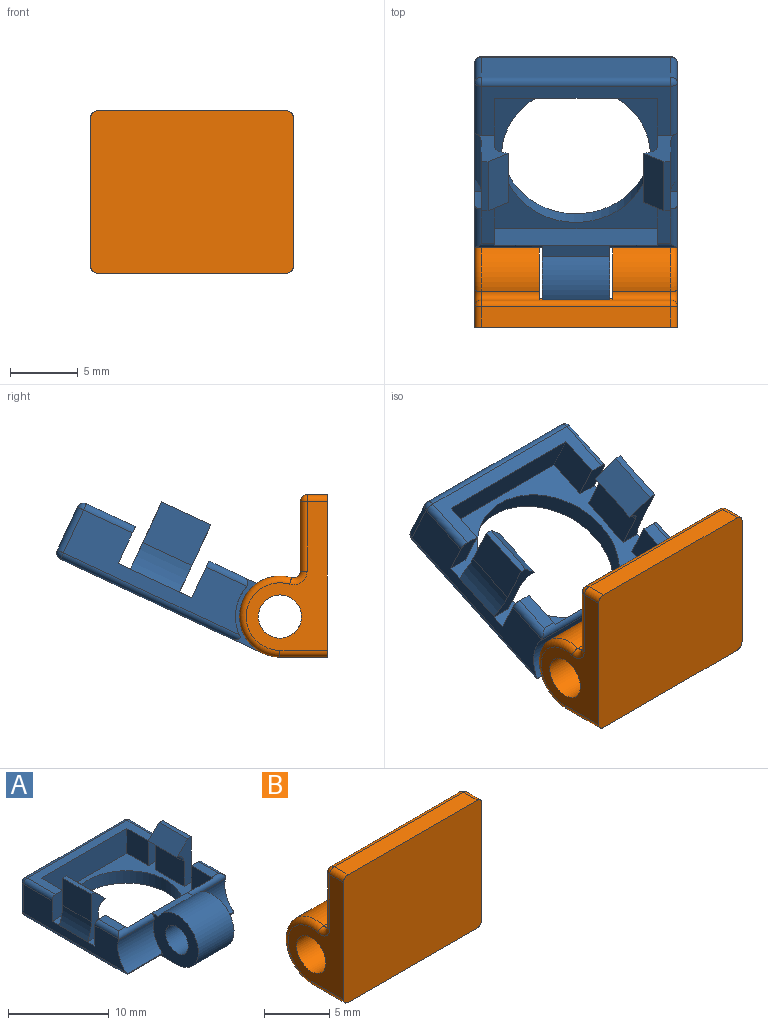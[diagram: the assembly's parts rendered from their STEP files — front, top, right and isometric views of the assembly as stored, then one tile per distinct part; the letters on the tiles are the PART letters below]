
ASSEMBLY  parts=2 mates=1
PART A: 60 faces, bbox 15x20x7 mm
  f0: plane 5x0.9mm, normal (0,0,1), area 4.5mm2, adj f2,f3,f15,f40
  f1: plane 2.83x1mm, normal (0,0,1), area 2.8mm2, adj f16,f27,f44,f45
  f2: plane 6.5x6mm, normal (-1,0,0), area 22.2mm2, adj f0,f15,f17,f38,f40,f41,f45,f59
  f3: plane 6.5x6mm, normal (1,0,0), area 22.2mm2, adj f0,f15,f17,f39,f40,f41,f43,f47
  f4: plane 2.83x1mm, normal (0,0,1), area 2.8mm2, adj f14,f23,f42,f43
  f5: plane 4x3mm, normal (1,0,0), area 12mm2, adj f19,f25,f28,f34
  f6: plane 4x3mm, normal (-1,0,0), area 12mm2, adj f19,f20,f22,f35
  f7: plane 14.35x3.5mm, normal (-1,0,0), area 32.1mm2, adj f19,f26,f27,f37,f38,f44,f45,f52
  f8: plane 3x3mm, normal (-1,0,0), area 9mm2, adj f10,f13,f19,f24
  f9: plane 3x3mm, normal (1,0,0), area 9mm2, adj f10,f13,f19,f26
  f10: plane 14x4mm, normal (0,0,1), area 20mm2, adj f8,f9,f13,f24,f26,f46,f51,f52
  f11: plane 14.35x3.5mm, normal (1,0,0), area 32.1mm2, adj f19,f23,f24,f36,f39,f42,f43,f46
  f12: plane 14x3.5mm, normal (0,1,0), area 49mm2, adj f50,f51,f55,f56
  f13: plane 12x3mm, normal (0,-1,0), area 36mm2, adj f8,f9,f10,f19
  f14: plane 3x3mm, normal (-1,0,0), area 9mm2, adj f4,f15,f19,f23,f43
  f15: plane 12x3mm, normal (0,1,0), area 35.8mm2, adj f0,f2,f3,f14,f16,f19,f43,f45
  f16: plane 3x3mm, normal (1,0,0), area 9mm2, adj f1,f15,f19,f27,f45
  f17: plane 16.5x14mm, normal (0,0,-1), area 113.6mm2, adj f2,f3,f18,f40,f47,f49,f55,f58
  f18: cylinder r=5.5mm len=11mm, axis (0,0,-1), area 51.8mm2, adj f17,f19
  f19: plane 15x12mm, normal (0,0,1), area 55mm2, adj f5,f6,f7,f8,f9,f11,f13,f14
  f20: plane 5.5x2.5mm, normal (0,1,0), area 6.4mm2, adj f6,f19,f21,f30,f32,f35,f36
  f21: plane 4x3.32mm, normal (1,0,0), area 13.3mm2, adj f20,f22,f30,f36
  f22: plane 5.5x2.5mm, normal (0,-1,0), area 6.4mm2, adj f6,f19,f21,f30,f32,f35,f36
  f23: plane 3x1.5mm, normal (0,1,0), area 4.4mm2, adj f4,f11,f14,f19,f42
  f24: plane 3x1.5mm, normal (0,-1,0), area 4.4mm2, adj f8,f10,f11,f19,f46
  f25: plane 5.5x2.5mm, normal (0,1,0), area 6.4mm2, adj f5,f19,f29,f31,f33,f34,f37
  f26: plane 3x1.5mm, normal (0,-1,0), area 4.4mm2, adj f7,f9,f10,f19,f52
  f27: plane 3x1.5mm, normal (0,1,0), area 4.4mm2, adj f1,f7,f16,f19,f44
  f28: plane 5.5x2.5mm, normal (0,-1,0), area 6.4mm2, adj f5,f19,f29,f31,f33,f34,f37
  f29: plane 4x3.32mm, normal (-1,0,0), area 13.3mm2, adj f25,f28,f31,f37
  f30: plane 4x0.5mm, normal (0,0,1), area 2mm2, adj f20,f21,f22,f32
  f31: plane 4x0.5mm, normal (0,0,1), area 2mm2, adj f25,f28,f29,f33
  f32: plane 4x1.5mm, normal (-0.71,0,0.71), area 8.5mm2, adj f20,f22,f30,f35
  f33: plane 4x1.5mm, normal (0.71,0,0.71), area 8.5mm2, adj f25,f28,f31,f34
  f34: cylinder r=1mm len=4mm, axis (0,-1,0), area 6.3mm2, adj f5,f25,f28,f33
  f35: cylinder r=1mm len=4mm, axis (0,-1,0), area 6.3mm2, adj f6,f20,f22,f32
  f36: cylinder r=5mm len=4mm, axis (0,-1,0), area 9mm2, adj f11,f20,f21,f22
  f37: cylinder r=5mm len=4mm, axis (0,-1,0), area 9mm2, adj f7,f25,f28,f29
  f38: cylinder r=3.3mm len=5mm, axis (1,0,0), area 19.6mm2, adj f2,f7,f45,f58,f59
  f39: cylinder r=3.3mm len=5mm, axis (-1,0,0), area 19.6mm2, adj f3,f11,f43,f47,f49
  f40: cylinder r=3mm len=6mm, axis (-1,0,0), area 62.8mm2, adj f0,f2,f3,f17
  f41: cylinder r=1.6mm len=5mm, axis (-1,0,0), area 50.3mm2, adj f2,f3
  f42: cylinder r=0.5mm len=3.33mm, axis (0,-1,0), area 2.5mm2, adj f4,f11,f23,f43
  f43: cylinder r=0.5mm len=5mm, axis (-1,0,0), area 3.9mm2, adj f3,f4,f11,f14,f15,f39,f42
  f44: cylinder r=0.5mm len=3.33mm, axis (0,1,0), area 2.5mm2, adj f1,f7,f27,f45
  f45: cylinder r=0.5mm len=5mm, axis (1,0,0), area 3.9mm2, adj f1,f2,f7,f15,f16,f38,f44
  f46: cylinder r=0.5mm len=4mm, axis (0,-1,0), area 3.1mm2, adj f10,f11,f24,f48
  f47: cylinder r=0.5mm len=4.98mm, axis (-1,0,0), area 3.2mm2, adj f3,f17,f39,f49
  f48: sphere r=0.5mm, area 0.4mm2, adj f46,f50,f51
  f49: cylinder r=0.5mm len=14.5mm, axis (0,1,0), area 11.2mm2, adj f11,f17,f39,f47,f53
  f50: cylinder r=0.5mm len=3.5mm, axis (0,0,-1), area 2.7mm2, adj f11,f12,f48,f53
  f51: cylinder r=0.5mm len=14mm, axis (1,0,0), area 11mm2, adj f10,f12,f48,f54
  f52: cylinder r=0.5mm len=4mm, axis (0,1,0), area 3.1mm2, adj f7,f10,f26,f54
  f53: sphere r=0.5mm, area 0.4mm2, adj f49,f50,f55
  f54: sphere r=0.5mm, area 0.4mm2, adj f51,f52,f56
  f55: cylinder r=0.5mm len=14mm, axis (-1,0,0), area 11mm2, adj f12,f17,f53,f57
  f56: cylinder r=0.5mm len=3.5mm, axis (0,0,1), area 2.7mm2, adj f7,f12,f54,f57
  f57: sphere r=0.5mm, area 0.4mm2, adj f55,f56,f58
  f58: cylinder r=0.5mm len=14.5mm, axis (0,-1,0), area 11.2mm2, adj f7,f17,f38,f57,f59
  f59: cylinder r=0.5mm len=4.98mm, axis (1,0,0), area 3.2mm2, adj f2,f17,f38,f58
PART B: 29 faces, bbox 15x6.7x12.2 mm
  f0: plane 6.35x6.3mm, normal (-1,0,0), area 22.5mm2, adj f1,f4,f8,f11,f12,f24,f28
  f1: plane 5.4x0.53mm, normal (0,0,-1), area 2.9mm2, adj f0,f8,f9,f28
  f2: plane 11x6mm, normal (-1,0,0), area 28.3mm2, adj f5,f7,f13,f14,f16,f17,f18
  f3: cylinder r=3mm len=6mm, axis (1,0,0), area 44.3mm2, adj f4,f9,f14,f15
  f4: plane 14x3.5mm, normal (0,0,-1), area 41.6mm2, adj f0,f3,f5,f9,f11,f13,f26,f28
  f5: plane 15x12mm, normal (0,-1,0), area 179.8mm2, adj f2,f4,f6,f10,f13,f17,f20,f26
  f6: plane 14x1.5mm, normal (0,0,1), area 21mm2, adj f5,f17,f20,f21
  f7: cylinder r=1.6mm len=4.8mm, axis (1,0,0), area 48.3mm2, adj f2,f9
  f8: plane 14x5.9mm, normal (0,1,0), area 76.1mm2, adj f0,f1,f9,f15,f18,f21,f23,f24
  f9: plane 6.35x6.3mm, normal (1,0,0), area 22.5mm2, adj f1,f3,f4,f7,f8,f15,f28
  f10: plane 11x6mm, normal (1,0,0), area 28.3mm2, adj f5,f12,f20,f23,f25,f26,f27
  f11: cylinder r=3mm len=6mm, axis (-1,0,0), area 44.3mm2, adj f0,f4,f24,f27
  f12: cylinder r=1.6mm len=4.8mm, axis (-1,0,0), area 48.3mm2, adj f0,f10
  f13: cylinder r=0.5mm len=3.5mm, axis (0,1,0), area 2.7mm2, adj f2,f4,f5,f14
  f14: torus R=2.5mm, axis (-1,0,0), area 7.6mm2, adj f2,f3,f13,f16
  f15: cylinder r=0.5mm len=4.3mm, axis (1,0,0), area 4mm2, adj f3,f8,f9,f16
  f16: torus R=1mm, axis (-1,0,0), area 1mm2, adj f2,f14,f15,f18
  f17: cylinder r=0.5mm len=1.5mm, axis (0,-1,0), area 1.2mm2, adj f2,f5,f6,f19
  f18: cylinder r=0.5mm len=5.15mm, axis (0,0,1), area 4mm2, adj f2,f8,f16,f19
  f19: sphere r=0.5mm, area 0.4mm2, adj f17,f18,f21
  f20: cylinder r=0.5mm len=1.5mm, axis (0,-1,0), area 1.2mm2, adj f5,f6,f10,f22
  f21: cylinder r=0.5mm len=14mm, axis (1,0,0), area 11mm2, adj f6,f8,f19,f22
  f22: sphere r=0.5mm, area 0.4mm2, adj f20,f21,f23
  f23: cylinder r=0.5mm len=5.15mm, axis (0,0,1), area 4mm2, adj f8,f10,f22,f25
  f24: cylinder r=0.5mm len=4.3mm, axis (-1,0,0), area 4mm2, adj f0,f8,f11,f25
  f25: torus R=1mm, axis (1,0,0), area 1mm2, adj f10,f23,f24,f27
  f26: cylinder r=0.5mm len=3.5mm, axis (0,1,0), area 2.7mm2, adj f4,f5,f10,f27
  f27: torus R=2.5mm, axis (1,0,0), area 7.6mm2, adj f10,f11,f25,f26
  f28: cylinder r=3.3mm len=5.6mm, axis (1,0,0), area 36.5mm2, adj f0,f1,f4,f9
PLACE A rot(axis=(1,0,0),25deg) t=(-6.36,8.82,3.91)mm
PLACE B t=(-6.36,8.45,-0.38)mm
MATE revolute A.f39 <-> B.f14  axis (-1,0,0) through (-8.86,-1.05,2.62)mm
